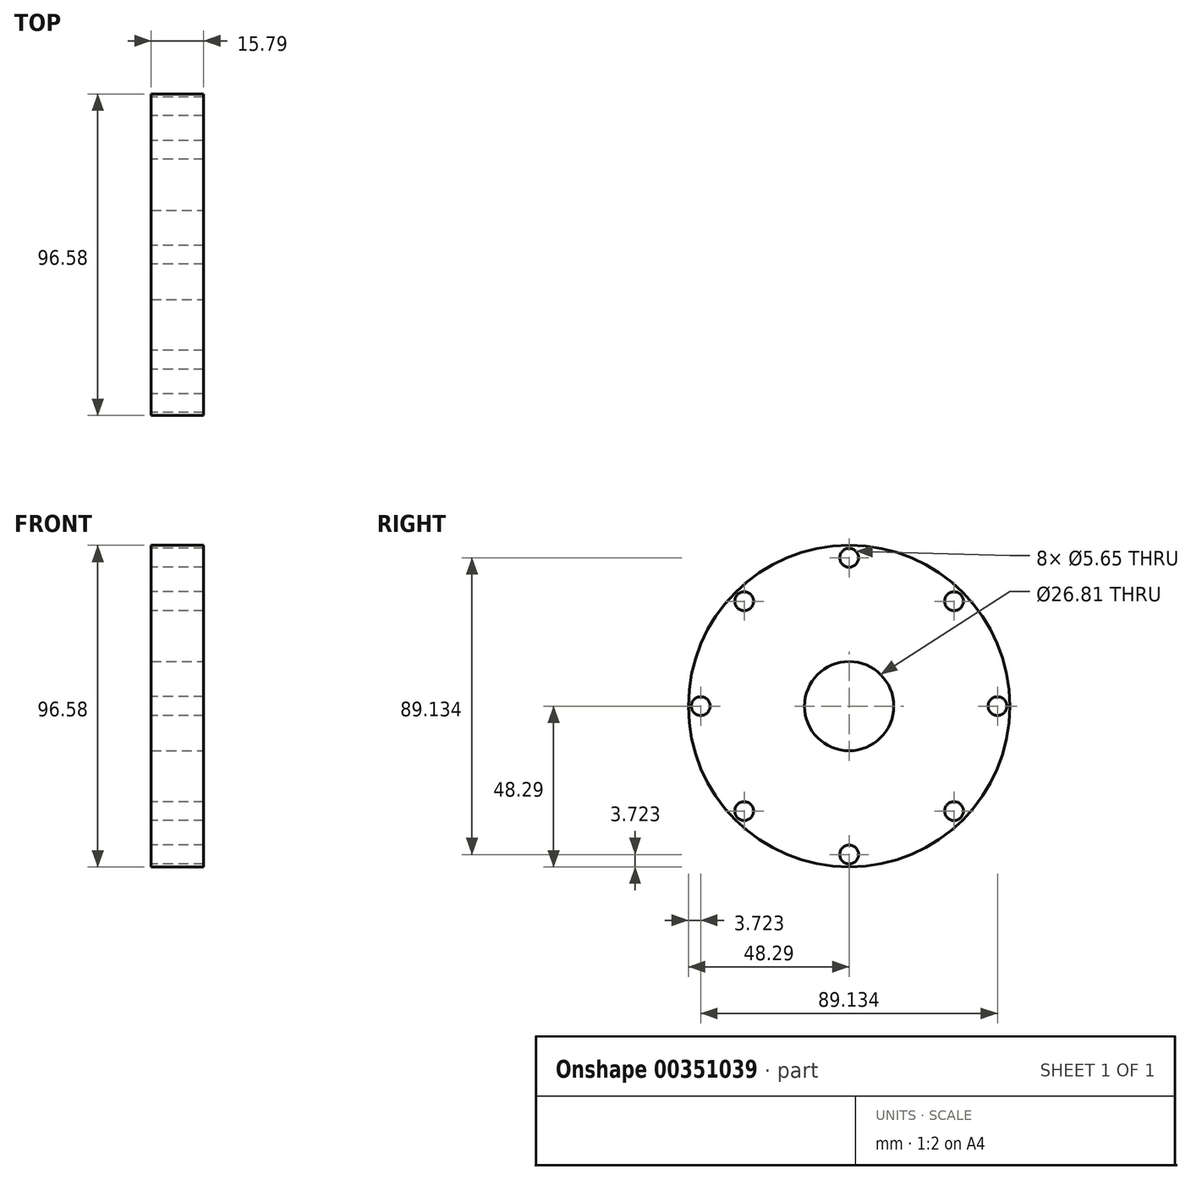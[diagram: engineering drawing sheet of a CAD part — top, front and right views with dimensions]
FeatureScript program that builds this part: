
annotation { "Feature Type Name" : "Feature", "Feature Type Description" : "" }
export const myFeature = defineFeature(function(context is Context, id is Id, definition is map)
    precondition{}
    {
        {
            var Q0;
            Q0=qCreatedBy(makeId("Front.planeOp"),FACE);
            var sketch = newSketch(context, id + "F0", { "sketchPlane" : qUnion([Q0])});
            skLineSegment(sketch, "E0.bottom", {"start": v(-8.45, 48.3) * mm, "end": v(7.34, 48.3) * mm});
            skLineSegment(sketch, "E0.top", {"start": v(-8.45, 13.4) * mm, "end": v(7.34, 13.4) * mm});
            skLineSegment(sketch, "E0.left", {"start": v(-8.45, 48.3) * mm, "end": v(-8.45, 13.4) * mm});
            skLineSegment(sketch, "E0.right", {"start": v(7.34, 48.3) * mm, "end": v(7.34, 13.4) * mm});
            skSolve(sketch);
        }
        {
            var Q0;
            Q0=qCreatedBy(makeId("Front.planeOp"),FACE);
            var sketch = newSketch(context, id + "F1", { "sketchPlane" : qUnion([Q0])});
            skLineSegment(sketch, "E1", {"start": v(0, 0) * mm, "end": v(-49.25, 0) * mm, "construction": true});
            skSolve(sketch);
        }
        {
            var Q0;
            Q0=makeQuery(id+"F0.imprint","IMPRINT",FACE,{"disambiguationData":[TD([[makeQuery(id+"F0.imprint","IMPRINT",EDGE,{"derivedFrom":sQuery(id+"F0.wireOp",EDGE,"E0.bottom")}),-1.0]])]});
            var Q1;
            Q1=sQuery(id+"F1.wireOp",EDGE,"E1");
            revolve(context, id + "F2", {"entities" : qUnion([Q0]), "axis" : qUnion([Q1]), "revolveType" : RevolveType.FULL});
        }
        {
            var Q0;
            Q0=makeQuery(id+"F2.opRevolve","SWEPT_FACE",FACE,{"disambiguationData":[OSD([sQuery(id+"F0.wireOp",EDGE,"E0.left")])]});
            var sketch = newSketch(context, id + "F3", { "sketchPlane" : qUnion([Q0])});
            skCircle(sketch, "E2", {"center": v(0, 44.57) * mm, "radius": 2.83 * mm});
            skSolve(sketch);
        }
        {
            var Q0;
            Q0=makeQuery(id+"F3.imprint","IMPRINT",FACE,{"disambiguationData":[TD([[makeQuery(id+"F3.imprint","IMPRINT",EDGE,{"derivedFrom":sQuery(id+"F3.wireOp",EDGE,"E2")}),1.0]])]});
            extrude(context, id + "F4", {"entities" : qUnion([Q0]), "operationType" : NewBodyOperationType.REMOVE, "oppositeDirection" : true, "depth" : 25.4 * mm});
        }
        {
            var Q0;
            Q0=makeQuery(id+"F4.boolean.opBoolean","COPY",FACE,{"derivedFrom":makeQuery(id+"F4.opExtrude","SWEPT_FACE",FACE,{"disambiguationData":[OSD([sQuery(id+"F3.wireOp",EDGE,"E2")])]})});
            var Q1;
            Q1=makeQuery(id+"F2.opRevolve","SWEPT_EDGE",EDGE,{"disambiguationData":[OSD([sQuery(id+"F0.wireOp",EDGE,"E0.bottom"),sQuery(id+"F0.wireOp",EDGE,"E0.left")])]});
            circularPattern(context, id + "F5", {"patternType" : PatternType.FACE, "faces" : qUnion([Q0]), "axis" : qUnion([Q1]), "angle" : 360 * degree, "instanceCount" : 8, "equalSpace" : true});
        }
    });
